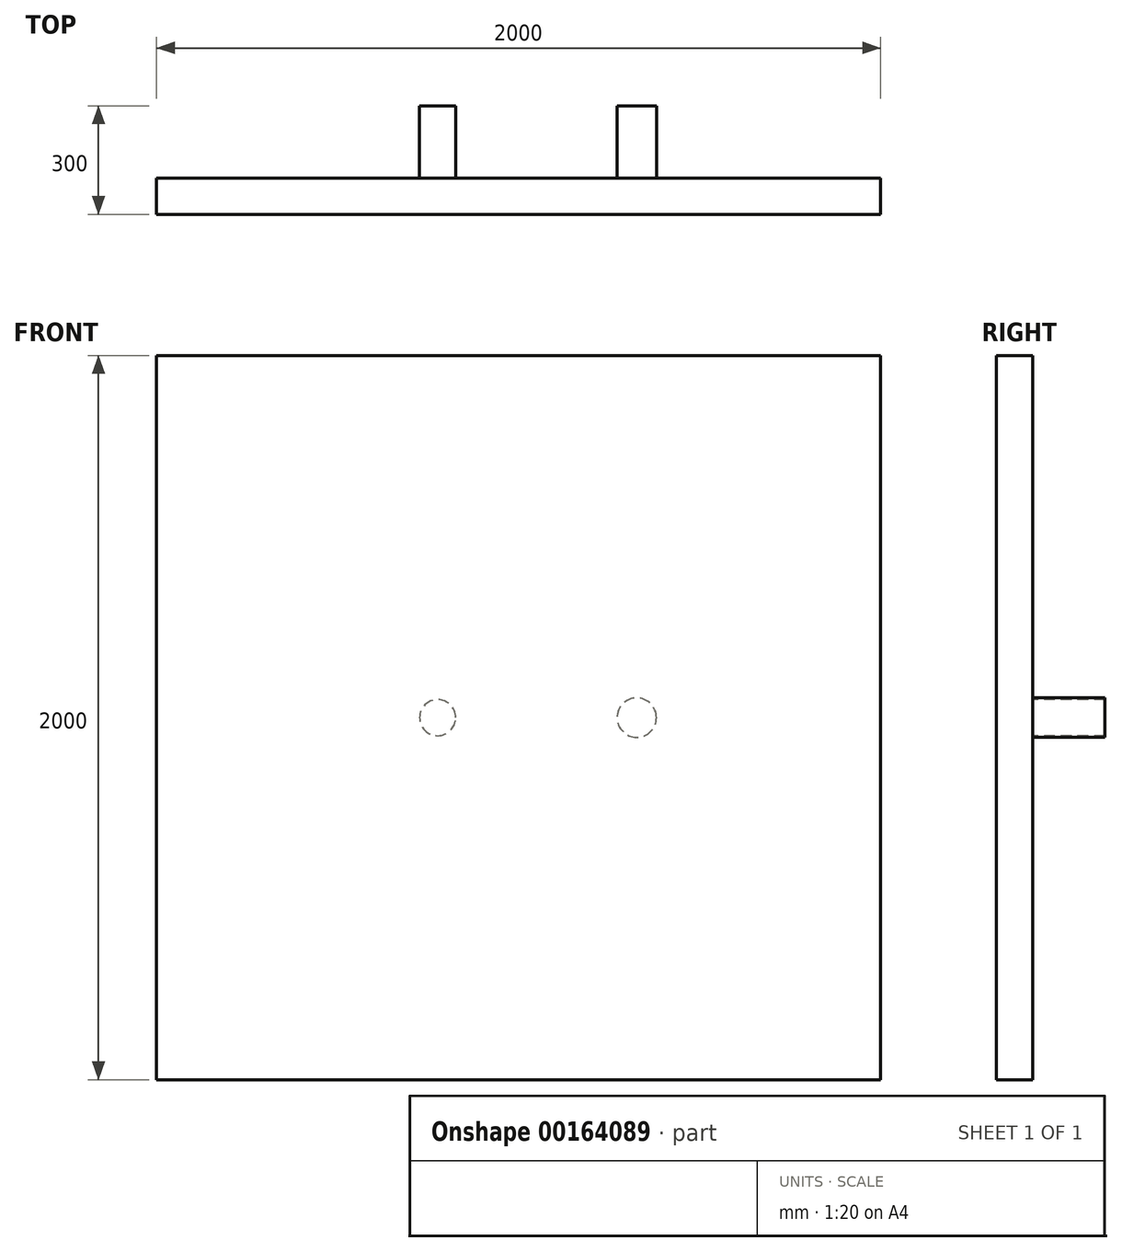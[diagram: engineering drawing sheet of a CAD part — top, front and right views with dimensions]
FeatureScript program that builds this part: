
annotation { "Feature Type Name" : "Feature", "Feature Type Description" : "" }
export const myFeature = defineFeature(function(context is Context, id is Id, definition is map)
    precondition{}
    {
        {
            var Q0;
            Q0=qCreatedBy(makeId("Front.planeOp"),FACE);
            var sketch = newSketch(context, id + "F0", { "sketchPlane" : qUnion([Q0])});
            skLineSegment(sketch, "E0.bottom", {"start": v(-1008.94, 1483.27) * mm, "end": v(991.06, 1483.27) * mm});
            skLineSegment(sketch, "E0.top", {"start": v(-1008.94, -516.73) * mm, "end": v(991.06, -516.73) * mm});
            skLineSegment(sketch, "E0.left", {"start": v(-1008.94, 1483.27) * mm, "end": v(-1008.94, -516.73) * mm});
            skLineSegment(sketch, "E0.right", {"start": v(991.06, 1483.27) * mm, "end": v(991.06, -516.73) * mm});
            skSolve(sketch);
        }
        {
            var Q0;
            Q0=makeQuery(id+"F0.imprint","IMPRINT",FACE,{"disambiguationData":[TD([[makeQuery(id+"F0.imprint","IMPRINT",EDGE,{"derivedFrom":sQuery(id+"F0.wireOp",EDGE,"E0.bottom")}),-1.0]])]});
            extrude(context, id + "F1", {"entities" : qUnion([Q0]), "depth" : 100 * mm});
        }
        {
            var Q0;
            Q0=makeQuery(id+"F1.opExtrude","CAP_FACE",FACE,{"disambiguationData":[OSD([sQuery(id+"F0.wireOp",EDGE,"E0.bottom"),sQuery(id+"F0.wireOp",EDGE,"E0.top"),sQuery(id+"F0.wireOp",EDGE,"E0.left"),sQuery(id+"F0.wireOp",EDGE,"E0.right")])],"isStart":false});
            var sketch = newSketch(context, id + "F2", { "sketchPlane" : qUnion([Q0])});
            skCircle(sketch, "E1", {"center": v(-232.2, 483.27) * mm, "radius": 50 * mm});
            skCircle(sketch, "E2", {"center": v(317.8, 483.27) * mm, "radius": 54.25 * mm});
            skSolve(sketch);
        }
        {
            var Q0;
            Q0 = qSketchRegion(id + "F2", true);
            extrude(context, id + "F3", {"entities" : qUnion([Q0]), "operationType" : NewBodyOperationType.ADD, "oppositeDirection" : true, "depth" : 300 * mm});
        }
    });
